# Revit family: IS_Tesi_T6630_BIM_IT
name_source: partatom
category: Plumbing Fixtures
revit_build: Autodesk Revit 2017 (Build: 20160225_1515(x64)
units: mm (PartAtom-declared; Revit-internal decimal feet)

## family parameters
Always vertical = No
Cut with Voids When Loaded = No
OmniClass Number = 23.45.05.21.11.11
OmniClass Title = Water Operated Water Closets
Part Type = Normal
Room Calculation Point = No
Round Connector Dimension = Use Diameter
Shared = No
Work Plane-Based = No

## types (1)
- T663001 - TESI CLASSIC SEAT & CVR WHITE
    Accessori = www.idealstandard.it
    AltezzaNominale = 58 mm
    BIMobject category = Toilet Seats
    BIMobject category code = sanitary-toilet-seats
    BIMobject main category = Sanitary
    BIMobject main category code = sanitary
    BOSUseNativeGeometries = 1
    Brand = Ideal Standard
    Brand url = http://www.idealstandard.it
    Caratteristiche = TESI CLASSIC SEAT & CVR WHITE
    CodiceABarre = 8014140321477
    CodiceDiPrestazione = EN
    Colore = Bianco
    Connessione = piombatura
    CostoDiSostituzione = 0 $
    Date of publishing = 2019_01_04
    Description = TESI CLASSIC SEAT & CVR WHITE
    Desrizione = TESI CLASSIC SEAT & CVR WHITE
    DimensioneScarico = 0
    EAN code = https://8014140321477
    Edition number = 1
    Finitura = Bianco
    Forma = scolpito
    Garanzia = Garanzia Ideal Standard
    GaranziaInstallazione = n/s
    Grado = n/s
    IFC Classification = IfcSanitaryTerminal
    IfcEsportaCome = SanitaryTerminal
    InformazioniDiProdotto = http://www.idealstandard.it
    Installation instructions = http://www.idealstandard.it
    Installazione = http://www.idealstandard.it
    InstruzioniInstallazione = http://www.idealstandard.it
    LarghezzaNominale = 0 mm  [stored 0 ft]
    LunghezzaNominale = 442 mm
    Maniglia = No
    Manufacturer name = Ideal Standard
    Material main = Acrylic
    Materiale = Acrilico
    Model = T663001
    NBS Reference Code = Pr_40_20_93_95
    NBS Reference Description = WC seats and covers
    Nominal depth = 0
    Nominal height = 0
    NominalDepth = 442 mm
    NominalHeight = 58 mm
    NominalLength = 442 mm
    NominalWidth = 363 mm
    NumeroDiModello = T504001
    OmniClass Code = 23-31 19 19 11
    OmniClass Description = Water Operated Water Closets
    PartiDiRicambio = http://www.idealstandard.it
    PiattoDoccia = No
    Product Guid = 2d6cb4fd-e6b3-44fd-b715-d492dd05e66e
    Product SKU = T6630
    Product certification = http://www.idealstandard.it
    Product data url = https://bimobject.com
    Product family = Sanitary
    Product group = Shower enclosures
    Product name = TESI CLASSIC SEAT & CVR WHITE
    Product url = http://www.idealstandard.it
    ProfonditaNominale = 0 mm  [stored 0 ft]
    QR code = http://bimobject.com
    Revisione = 1
    SeatMaterial = 0 mm  [stored 0 ft]
    Size = 363 x 442 x 58 mm
    SpessoreDelMateriale = 0
    SpilloverLivello = 0
    Technical description = http://www.idealstandard.it
    Telefono = 800 652 290
    TipoDiDato = Fisso
    TipoEspotazioneIfc = IfcSanitaryTerminalType
    URL = http://www.idealstandard.it
    Uniclass 1.4 Code = L72164
    Uniclass 1.4 Description = WC cisterns
    Uniclass 2.0 Code = PR-35-93-95
    Uniclass 2.0 Description = Wc Seats And Covers
    Uniclass 2015 Code = Pr_40_20_93_95
    Uniclass 2015 Name = WC seats and covers
    UnitàDurata = anni
    UnitàDurataGaranzia = anni
    UnitàLineare = millimetri
    UnitàMonetaria = €
    UnitàSuperficie = €
    UnitàVolume = millimetri
    Versione = 1
    VersioneClassificazioneUni2015 = 1
    Weight Net (Kg) = 0
    Youtube clip = https://www.youtube.com

note: [stored X ft] marks values corroborated as IEEE doubles in the binary element streams (Revit-internal decimal feet)

## geometry (parser evidence)
native form markers: Sweep x1
no freeform markers — native parametric forms only
